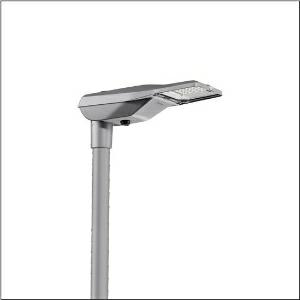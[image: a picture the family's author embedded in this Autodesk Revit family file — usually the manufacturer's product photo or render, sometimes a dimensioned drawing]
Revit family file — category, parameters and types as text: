
# Revit family: streetlight_sl_21_micro___st1_0a_5xe1d33r08db_e2a0
name_source: partatom
category: Lighting Fixtures
units: mm (PartAtom-declared; Revit-internal decimal feet)

## family parameters
Cut with Voids When Loaded = No
Host = Face
Light Source = No
Part Type = Normal
Room Calculation Point = No
Round Connector Dimension = Use Diameter
Shared = No

## types (1)
- --- (1 x LED, 5110 lm, 39.1 W, 3000K)
    Apparent Load = 39 VA
    CIE Flux Codes = 37 72 97 100 100
    Color Rendering = 70
    Color Temperature = 3000K
    Default Elevation = 1800 mm
    Description = Streetlight SL 21 micro, mast luminaire, primary light control with lens, of PMMA, primary optical cover: cover, of toughened safety glass, transparent, light distribution: ST1.0a, light emission: direct distribution, primary light characteristic: asymmetric, installation type: side-entry, post-top, LED, High Power LED, rated luminous flux: 5.110lm, luminous efficacy: 131lm/W, light colour: 730, colour temperature: 3000K, control gear: D4i, control: flexible luminous flux parameterisation, time-dependent luminous flux control, constant luminous flux control, overheat protection, pre-setting: logarithmic dimming characteristic, mains connection: 220..240V, AC, 50/60Hz, start of lifetime: 39W, end of service life: 41W, reduction: 18W, luminaire housing, of diecast aluminium, powder-coated, Siteco® metallic grey (DB 702S), corrosivity category C5 mid according to DIN EN ISO 12944, please order mast flange separately, inclination adjustable: 0°, 5°, 10°, 15°, sealing non-destructively replaceable, multi-level sealing system, length: 528mm, width: 235mm, height: 110mm, mast flange for spigot size: 42mm (side-entry): 5XC10008XM4, 60/48mm (side-entry/post-top): 5XC10108XM2, 76/60mm (side-entry/post-top): 5XC10108XM1, Smart Interface below, protection rating (complete): IP66, insulation class (complete): insulation class II (safety insulation), certification: CE, ENEC, ENEC+, VDE, impact resistance: IK10, permissible operating ambient temperature for outdoor applications: -40..+50°C, standard-compliant lighting for roads and squares, packaging unit: 1 piece

Light Distribution: ST1.0a
    Height = 110 mm
    Lamp = 1 x LED
    Lamp Light Flux = 5110 lm
    Lamp Power = 39.1 W
    Lamp count = 1
    Length = 528 mm
    Luminous efficacy = 131 lm/W
    Manufacturer = Siteco
    ModVariant = No
    Model = 5XE1D33R08DB
    Number of Poles = 1
    OnlyDefault = Yes
    Power Factor = 1
    Product Name = Streetlight SL 21 micro | ST1.0a
    Product group = mast luminaire | pylon top
    ProductGroupID = 6100
    Protection Class = Protection class II
    Protection Degree = IP 66
    RLX_Detail_Level = 1
    RLX_Emergency_Light_Flux = 0 lm
    RLX_Emergency_Type = 0
    RLX_Emergency_Type_DB = No
    RlxData = <blob elided: 98589 chars, md5=1acce3ee>
    Socket = socket
    Standby Power = 0 W
    System Light Flux = 5110 lm
    System Power = 39 W
    Type Comments = factory setting: luminous flux: 100 % | dim-lin: 254 | 765 mA
    Type Image = l_1277290.jpg
    URL = http://relux.com
    VarID = @adj_155912
    Voltage = 0 V
    Weight = 0.00 kg
    Width = 235 mm

## geometry (parser evidence)
native form markers: Blend x4, Sweep x11
no freeform markers — native parametric forms only
